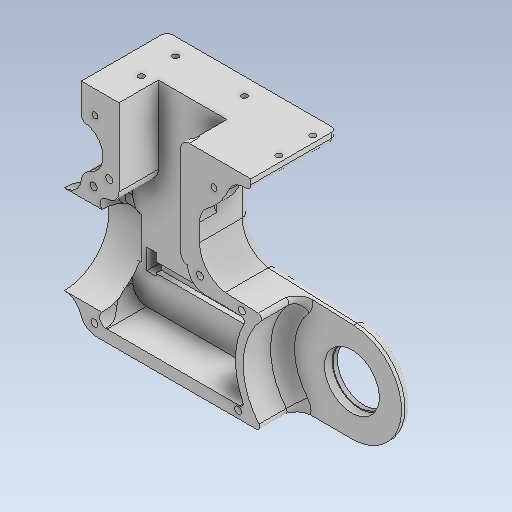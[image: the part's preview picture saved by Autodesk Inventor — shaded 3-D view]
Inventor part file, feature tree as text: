
AUTODESK INVENTOR PART (.ipt)
format: ipt  version: 2020 (Build 240168000, 168)  size: 915,968 bytes
history: native  units: mm
features: sketch x7, other x6, extrude x5, hole x2, projected_geometry x2, reference x1
ambient origin geometry x8: Origin, YZ Plane, XZ Plane, XY Plane, X Axis, Y Axis, Z Axis, Center Point
bodies: Solid1 (feature_tree)
feature tree (23):
  other  "bodyL.ipt"
  extrude  "Extrusion1"  Depth=52.0mm
  extrude  "Extrusion3"  Depth=10.0mm
  extrude  "Extrusion4"  Depth=32.08mm
  extrude  "Extrusion5"  Depth=31.0mm
  hole  "Hole1"  [1 undecoded]
  hole  "Hole2"  [1 undecoded]
  extrude  "Extrusion6"  [1 undecoded]
  other  "Solid1::bodyL.ipt"
  other  "TaggingFeature2"
  sketch  "Sketch1"  dims[d1=10.0mm]
  sketch  "Sketch3"  dims[d4=54.0mm d6=58.0mm d7=15.0mm d8=65.0mm d9=30.0mm d10=0.0mm d12=120.0mm d14=15.0mm d15=80.0mm d16=52.0mm d17=60.0mm d19=24.0mm d20=0.0mm d21=7.0mm d22=40.0mm d23=20.0mm d24=0.0mm d25=25.0mm d26=3.4mm d28=6.3mm d30=90.0deg d31=20.0mm d46=81.0mm d48=0.0mm d49=25.0mm d50=3.4mm d52=6.3mm d54=90.0deg d55=20.0mm d57=11.0mm d59=0.0mm d2=52.0mm]
  sketch  "Sketch4"  dims[d3=10.0mm d5=0.0mm d41=40.0mm]
  sketch  "Sketch5"  dims[d43=7.0mm d47=0.0mm d51=32.08mm]
  reference  "Reference1"
  sketch  "Sketch6"  dims[d53=7.0mm d56=0.0mm d58=31.0mm]
  projected_geometry  "Projected Loop2"
  sketch  "Sketch7"  dims[d60=2.5mm d61=0.0mm]
  projected_geometry  "Projected Loop3"
  sketch  "Sketch8"  dims[d62=3.4mm d63=6.0mm d64=6.3mm d65=2.0mm d66=90.0deg d67=8.0mm d68=20.594885mm d69=3.4mm d70=6.0mm d71=6.3mm d72=2.0mm d73=90.0deg d74=8.0mm d75=20.594885mm d76=10.0mm d77=0.0mm]
  other  "<userpath>\Desktop\KangKangBalancing\KangKang.iam"
  other  "KangKang.iam"
  other  "front wheel:1"
note: 3 required parameter values undecoded (feature->parameter linkage not recoverable at this tier; creation-order binding heuristic only, values carry confidence <= 0.55)
